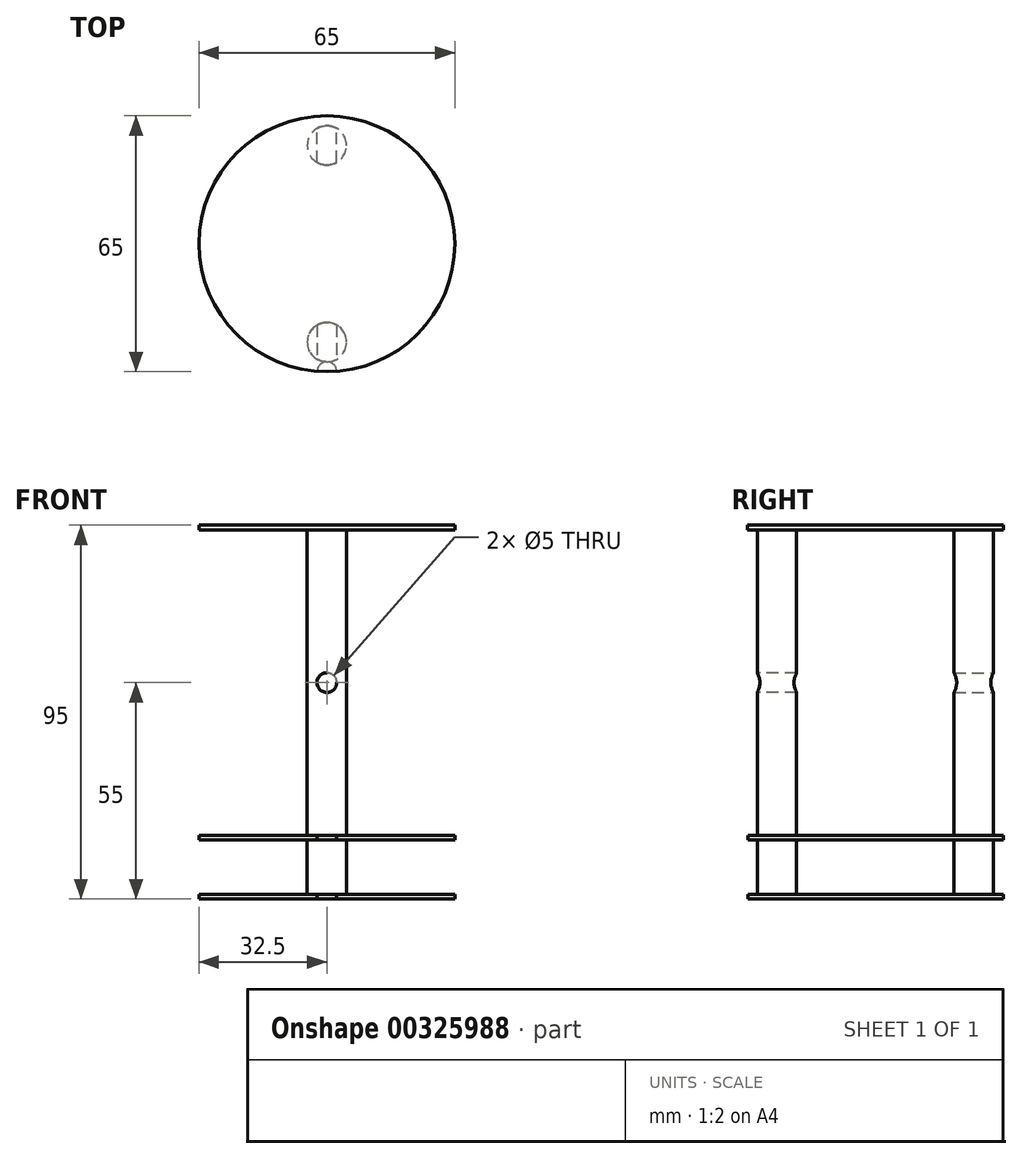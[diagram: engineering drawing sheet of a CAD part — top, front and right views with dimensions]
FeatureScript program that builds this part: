
annotation { "Feature Type Name" : "Feature", "Feature Type Description" : "" }
export const myFeature = defineFeature(function(context is Context, id is Id, definition is map)
    precondition{}
    {
        {
            var Q0;
            Q0=qCreatedBy(makeId("Top.planeOp"),FACE);
            var sketch = newSketch(context, id + "F0", { "sketchPlane" : qUnion([Q0])});
            skCircle(sketch, "E0", {"center": v(0, 0) * mm, "radius": 32.5 * mm});
            skLineSegment(sketch, "E1", {"start": v(0, 32.5) * mm, "end": v(0, -32.5) * mm, "construction": true});
            skCircle(sketch, "E2", {"center": v(0, 25) * mm, "radius": 5 * mm});
            skCircle(sketch, "E3.1.0", {"center": v(0, -25) * mm, "radius": 5 * mm});
            skSolve(sketch);
        }
        {
            var Q0;
            Q0=makeQuery(id+"F0.imprint","IMPRINT",FACE,{"disambiguationData":[TD([[makeQuery(id+"F0.imprint","IMPRINT",EDGE,{"derivedFrom":sQuery(id+"F0.wireOp",EDGE,"E0")}),1.0]])]});
            extrude(context, id + "F1", {"entities" : qUnion([Q0]), "depth" : 80 * mm, "offsetDistance" : 25 * mm, "hasSecondDirection" : true, "secondDirectionOppositeDirection" : false, "secondDirectionDepth" : 78.8 * mm});
        }
        {
            var Q0;
            Q0=makeQuery(id+"F0.imprint","IMPRINT",FACE,{"disambiguationData":[TD([[makeQuery(id+"F0.imprint","IMPRINT",EDGE,{"derivedFrom":sQuery(id+"F0.wireOp",EDGE,"E2")}),1.0]])]});
            var Q1;
            Q1=makeQuery(id+"F0.imprint","IMPRINT",FACE,{"disambiguationData":[TD([[makeQuery(id+"F0.imprint","IMPRINT",EDGE,{"derivedFrom":sQuery(id+"F0.wireOp",EDGE,"E3.1.0")}),1.0]])]});
            extrude(context, id + "F2", {"entities" : qUnion([Q0, Q1]), "operationType" : NewBodyOperationType.ADD, "depth" : 80 * mm, "offsetDistance" : 25 * mm, "hasSecondDirection" : true, "secondDirectionOppositeDirection" : true, "secondDirectionDepth" : 15 * mm});
        }
        {
            var Q0;
            Q0=makeQuery(id+"F0.imprint","IMPRINT",FACE,{"disambiguationData":[TD([[makeQuery(id+"F0.imprint","IMPRINT",EDGE,{"derivedFrom":sQuery(id+"F0.wireOp",EDGE,"E0")}),1.0]])]});
            extrude(context, id + "F3", {"entities" : qUnion([Q0]), "operationType" : NewBodyOperationType.ADD, "depth" : 1.2 * mm, "offsetDistance" : 25 * mm});
        }
        {
            var Q0;
            Q0=makeQuery(id+"F0.imprint","IMPRINT",FACE,{"disambiguationData":[TD([[makeQuery(id+"F0.imprint","IMPRINT",EDGE,{"derivedFrom":sQuery(id+"F0.wireOp",EDGE,"E0")}),1.0]])]});
            extrude(context, id + "F4", {"entities" : qUnion([Q0]), "operationType" : NewBodyOperationType.ADD, "oppositeDirection" : true, "depth" : 15 * mm, "offsetDistance" : 25 * mm, "hasSecondDirection" : true, "secondDirectionOppositeDirection" : true, "secondDirectionDepth" : 13.8 * mm});
        }
        {
            var Q0;
            Q0=sQuery(id+"F0.wireOp",VERTEX,"E1.end");
            var Q1;
            Q1=makeQuery(id+"F1.opExtrude","SWEPT_BODY",BODY,{"disambiguationData":[OSD([sQuery(id+"F0.wireOp",EDGE,"E0"),sQuery(id+"F0.wireOp",EDGE,"E2"),sQuery(id+"F0.wireOp",EDGE,"E3.1.0")])]});
            hole(context, id + "F5", {"style" : HoleStyle.SIMPLE, "endStyle" : HoleEndStyle.THROUGH, "holeDiameter" : 5 * mm, "majorDiameter" : 5 * mm, "tappedDepth" : 12 * mm, "tapClearance" : 3, "locations" : qUnion([Q0]), "scope" : qUnion([Q1]), "startStyle" : HoleStartStyle.PART});
        }
        {
            var Q0;
            Q0=sQuery(id+"F0.wireOp",VERTEX,"E1.end");
            var Q1;
            Q1=makeQuery(id+"F1.opExtrude","SWEPT_BODY",BODY,{"disambiguationData":[OSD([sQuery(id+"F0.wireOp",EDGE,"E0"),sQuery(id+"F0.wireOp",EDGE,"E2"),sQuery(id+"F0.wireOp",EDGE,"E3.1.0")])]});
            hole(context, id + "F6", {"style" : HoleStyle.SIMPLE, "endStyle" : HoleEndStyle.BLIND, "oppositeDirection" : true, "holeDiameter" : 5 * mm, "majorDiameter" : 5 * mm, "holeDepth" : 12 * mm, "tappedDepth" : 12 * mm, "tapClearance" : 3, "locations" : qUnion([Q0]), "scope" : qUnion([Q1]), "startStyle" : HoleStartStyle.PART});
        }
        {
            var Q0;
            Q0=qCreatedBy(makeId("Front.planeOp"),FACE);
            var sketch = newSketch(context, id + "F7", { "sketchPlane" : qUnion([Q0])});
            skLineSegment(sketch, "E4", {"start": v(-5, -13.8) * mm, "end": v(-5, 0) * mm});
            skLineSegment(sketch, "E5", {"start": v(5, 0) * mm, "end": v(5, -13.8) * mm});
            skLineSegment(sketch, "E6", {"start": v(-5, 1.2) * mm, "end": v(-5, 78.8) * mm});
            skLineSegment(sketch, "E7", {"start": v(5, 78.8) * mm, "end": v(5, 1.2) * mm});
            skPoint(sketch, "E8", {"position": v(5, 40) * mm});
            skPoint(sketch, "E9", {"position": v(-5, 40) * mm});
            skLineSegment(sketch, "E10", {"start": v(-5, 40) * mm, "end": v(5, 40) * mm, "construction": true});
            skPoint(sketch, "E11", {"position": v(0, 40) * mm});
            skSolve(sketch);
        }
        {
            var Q0;
            Q0=sQuery(id+"F7.wireOp",VERTEX,"E11");
            var Q1;
            Q1=makeQuery(id+"F1.opExtrude","SWEPT_BODY",BODY,{"disambiguationData":[OSD([sQuery(id+"F0.wireOp",EDGE,"E0"),sQuery(id+"F0.wireOp",EDGE,"E2"),sQuery(id+"F0.wireOp",EDGE,"E3.1.0")])]});
            hole(context, id + "F8", {"style" : HoleStyle.SIMPLE, "endStyle" : HoleEndStyle.THROUGH, "holeDiameter" : 5 * mm, "majorDiameter" : 5 * mm, "tappedDepth" : 12 * mm, "tapClearance" : 3, "locations" : qUnion([Q0]), "scope" : qUnion([Q1]), "startStyle" : HoleStartStyle.PART});
        }
        {
            var Q0;
            Q0=sQuery(id+"F7.wireOp",VERTEX,"E11");
            var Q1;
            Q1=makeQuery(id+"F1.opExtrude","SWEPT_BODY",BODY,{"disambiguationData":[OSD([sQuery(id+"F0.wireOp",EDGE,"E0"),sQuery(id+"F0.wireOp",EDGE,"E2"),sQuery(id+"F0.wireOp",EDGE,"E3.1.0")])]});
            hole(context, id + "F9", {"style" : HoleStyle.SIMPLE, "endStyle" : HoleEndStyle.THROUGH, "oppositeDirection" : true, "holeDiameter" : 5 * mm, "majorDiameter" : 5 * mm, "tappedDepth" : 12 * mm, "tapClearance" : 3, "locations" : qUnion([Q0]), "scope" : qUnion([Q1]), "startStyle" : HoleStartStyle.PART});
        }
    });
